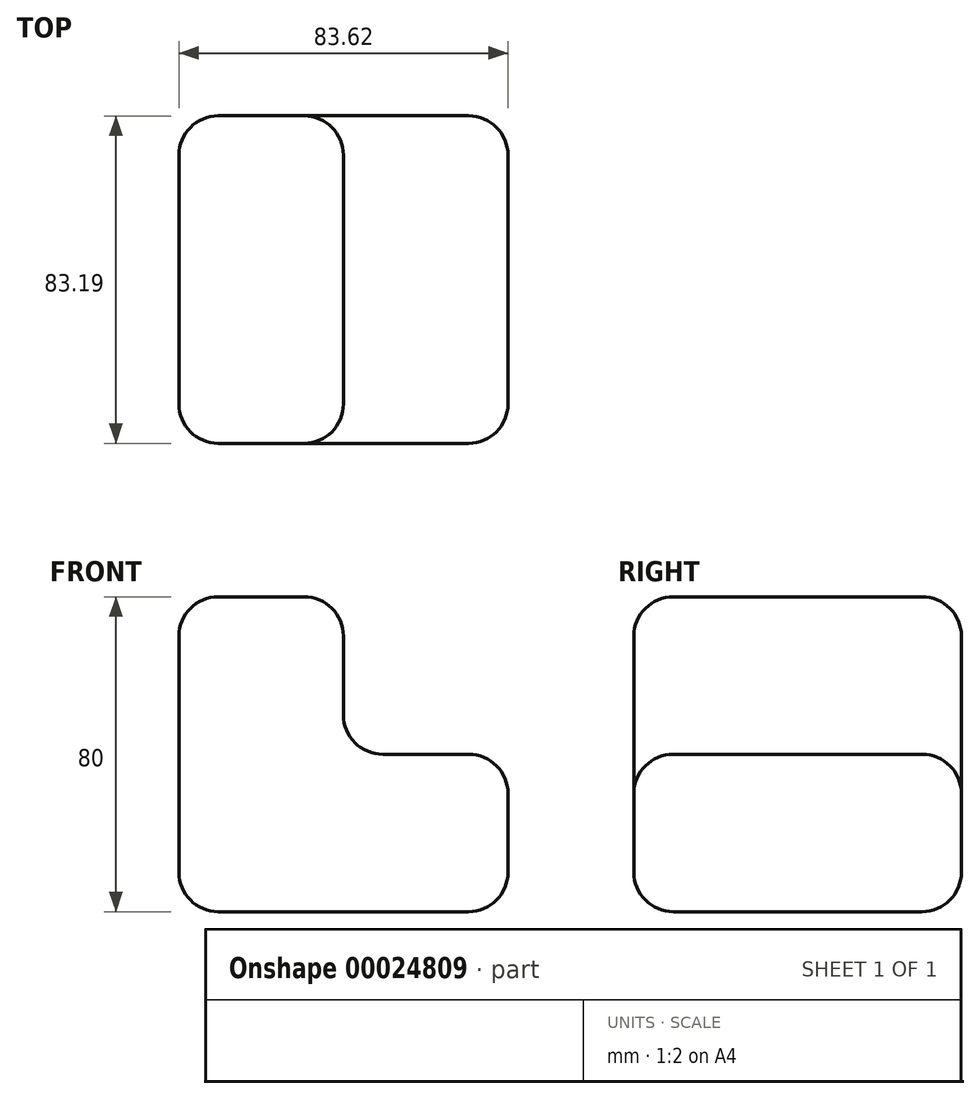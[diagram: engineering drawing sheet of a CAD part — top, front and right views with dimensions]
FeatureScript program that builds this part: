
annotation { "Feature Type Name" : "Feature", "Feature Type Description" : "" }
export const myFeature = defineFeature(function(context is Context, id is Id, definition is map)
    precondition{}
    {
        {
            var Q0;
            Q0=qCreatedBy(makeId("Top.planeOp"),FACE);
            var sketch = newSketch(context, id + "F0", { "sketchPlane" : qUnion([Q0])});
            skLineSegment(sketch, "E0.bottom", {"start": v(-59.13, -45.93) * mm, "end": v(24.5, -45.93) * mm});
            skLineSegment(sketch, "E0.top", {"start": v(-59.13, 37.26) * mm, "end": v(24.5, 37.26) * mm});
            skLineSegment(sketch, "E0.left", {"start": v(-59.13, -45.93) * mm, "end": v(-59.13, 37.26) * mm});
            skLineSegment(sketch, "E0.right", {"start": v(24.5, -45.93) * mm, "end": v(24.5, 37.26) * mm});
            skSolve(sketch);
        }
        {
            var Q0;
            Q0=makeQuery(id+"F0.imprint","IMPRINT",FACE,{"disambiguationData":[TD([[makeQuery(id+"F0.imprint","IMPRINT",EDGE,{"derivedFrom":sQuery(id+"F0.wireOp",EDGE,"E0.bottom")}),1.0]])]});
            extrude(context, id + "F1", {"entities" : qUnion([Q0]), "depth" : 40 * mm});
        }
        {
            var Q0;
            Q0=makeQuery(id+"F1.opExtrude","CAP_FACE",FACE,{"disambiguationData":[OSD([sQuery(id+"F0.wireOp",EDGE,"E0.bottom"),sQuery(id+"F0.wireOp",EDGE,"E0.top"),sQuery(id+"F0.wireOp",EDGE,"E0.left"),sQuery(id+"F0.wireOp",EDGE,"E0.right")])],"isStart":false});
            var sketch = newSketch(context, id + "F2", { "sketchPlane" : qUnion([Q0])});
            skLineSegment(sketch, "E1", {"start": v(-17.32, 37.26) * mm, "end": v(-17.32, -45.93) * mm});
            skSolve(sketch);
        }
        {
            var Q0;
            {var subQ1=sQuery(id+"F2.wireOp",EDGE,"E1");Q0=makeQuery(id+"F2.imprint","IMPRINT",FACE,{"disambiguationData":[TD([[makeQuery(id+"F2.imprint","IMPRINT",EDGE,{"derivedFrom":subQ1}),-1.0]])]});}
            extrude(context, id + "F3", {"entities" : qUnion([Q0]), "operationType" : NewBodyOperationType.ADD, "depth" : 40 * mm});
        }
        {
            var Q0;
            Q0=makeQuery(id+"F3.opExtrude","CAP_EDGE",EDGE,{"disambiguationData":[OSD([sQuery(id+"F2.wireOp",EDGE,"E1")])],"isStart":false});
            var Q1;
            Q1=makeQuery(id+"F3.opExtrude","CAP_FACE",FACE,{"disambiguationData":[OSD([sQuery(id+"F0.wireOp",EDGE,"E0.bottom"),sQuery(id+"F0.wireOp",EDGE,"E0.top"),sQuery(id+"F0.wireOp",EDGE,"E0.left"),sQuery(id+"F2.wireOp",EDGE,"E1")])],"isStart":false});
            var Q2;
            Q2=makeQuery(id+"F1.opExtrude","CAP_FACE",FACE,{"disambiguationData":[OSD([sQuery(id+"F0.wireOp",EDGE,"E0.bottom"),sQuery(id+"F0.wireOp",EDGE,"E0.top"),sQuery(id+"F0.wireOp",EDGE,"E0.left"),sQuery(id+"F0.wireOp",EDGE,"E0.right")])],"isStart":false});
            var Q3;
            {var subQ0=sQuery(id+"F0.wireOp",EDGE,"E0.bottom");Q3=makeQuery(id+"F3.boolean.opBoolean","MERGE",FACE,{"derivedFrom":[makeQuery(id+"F1.opExtrude","SWEPT_FACE",FACE,{"disambiguationData":[OSD([subQ0])]}),makeQuery(id+"F3.opExtrude","SWEPT_FACE",FACE,{"disambiguationData":[OSD([subQ0])]})]});}
            var Q4;
            Q4=makeQuery(id+"F1.opExtrude","SWEPT_FACE",FACE,{"disambiguationData":[OSD([sQuery(id+"F0.wireOp",EDGE,"E0.right")])]});
            var Q5;
            {var subQ0=sQuery(id+"F0.wireOp",EDGE,"E0.top");Q5=makeQuery(id+"F3.boolean.opBoolean","MERGE",FACE,{"derivedFrom":[makeQuery(id+"F1.opExtrude","SWEPT_FACE",FACE,{"disambiguationData":[OSD([subQ0])]}),makeQuery(id+"F3.opExtrude","SWEPT_FACE",FACE,{"disambiguationData":[OSD([subQ0])]})]});}
            var Q6;
            Q6=makeQuery(id+"F1.opExtrude","CAP_FACE",FACE,{"disambiguationData":[OSD([sQuery(id+"F0.wireOp",EDGE,"E0.bottom"),sQuery(id+"F0.wireOp",EDGE,"E0.top"),sQuery(id+"F0.wireOp",EDGE,"E0.left"),sQuery(id+"F0.wireOp",EDGE,"E0.right")])],"isStart":true});
            fillet(context, id + "F4", {"entities" : qUnion([Q0, Q1, Q2, Q3, Q4, Q5, Q6]), "radius" : 10 * mm, "tangentPropagation" : true, "allowEdgeOverflow" : false});
        }
    });
